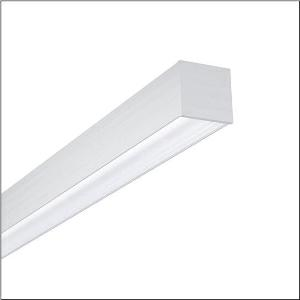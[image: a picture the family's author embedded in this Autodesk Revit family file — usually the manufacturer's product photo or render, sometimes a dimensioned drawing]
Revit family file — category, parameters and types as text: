
# Revit family: silica_r_5mx22wd1e4a_75c3
name_source: partatom
category: Lighting Fixtures
units: mm (PartAtom-declared; Revit-internal decimal feet)

## family parameters
Cut with Voids When Loaded = No
Host = Face
Light Source = No
Part Type = Normal
Room Calculation Point = No
Round Connector Dimension = Use Diameter
Shared = No

## types (1)
- --- (1 x LED, 4680 lm, 29.3 W, 4000K)
    Apparent Load = 29 VA
    CIE Flux Codes = 70 95 99 100 100
    Color Rendering = 80
    Color Temperature = 4000K
    Default Elevation = 1800 mm
    Description = Silica®, office luminaire, primary light control with wallwasher, of aluminium, light emission: direct distribution, primary light characteristic: asymmetric, installation type: surface-mounted, LED, rated luminous flux: 4.680lm, luminous efficacy: 160lm/W, light colour: 840, colour temperature: 4000K, control gear: ECG DALI, with terminal, 3+2-pole, max. 2.5mm², mains connection: 230V, AC, 50/60Hz, rated input power: 29W, luminaire housing, of aluminium, anodised, silver, length: 1.442mm, width: 65mm, height: 64mm, protection rating (complete): IP20, insulation class (complete): insulation class I (protective earthing), certification: CE, permissible operating ambient temperature: 0..+35°C, standard: EN 50419, packaging unit: 1 piece
    Height = 64 mm
    Lamp = 1 x LED
    Lamp Light Flux = 4680 lm
    Lamp Power = 29.3 W
    Lamp count = 1
    Length = 1442 mm
    Luminous efficacy = 160 lm/W
    Manufacturer = Siteco
    ModVariant = No
    Model = 5MX22WD1E4A
    Mounting Place = Ceiling
    Mounting Type = Surface mounted
    Number of Poles = 1
    OnlyDefault = Yes
    Power Factor = 1
    Product Name = Silica®
    Product group = office luminaire | ceiling mounted
    ProductGroupID = 304
    Protection Class = Protection class I
    Protection Degree = IP 20
    RLX_Detail_Level = 1
    RLX_Emergency_Light_Flux = 0 lm
    RLX_Emergency_Type = 0
    RLX_Emergency_Type_DB = No
    RlxData = <blob elided: 27853 chars, md5=35238045>
    Socket = socket
    Standby Power = 0 W
    System Light Flux = 4680 lm
    System Power = 29 W
    Type Comments = factory setting: luminous flux: 100 % | dim-lin: 254 | 164 mA
    Type Image = l_1004827.jpg
    URL = http://relux.com
    VarID = @adj_138218
    Voltage = 0 V
    Weight = 0.00 kg
    Width = 66 mm

## geometry (parser evidence)
native form markers: Blend x4, Sweep x11
no freeform markers — native parametric forms only
